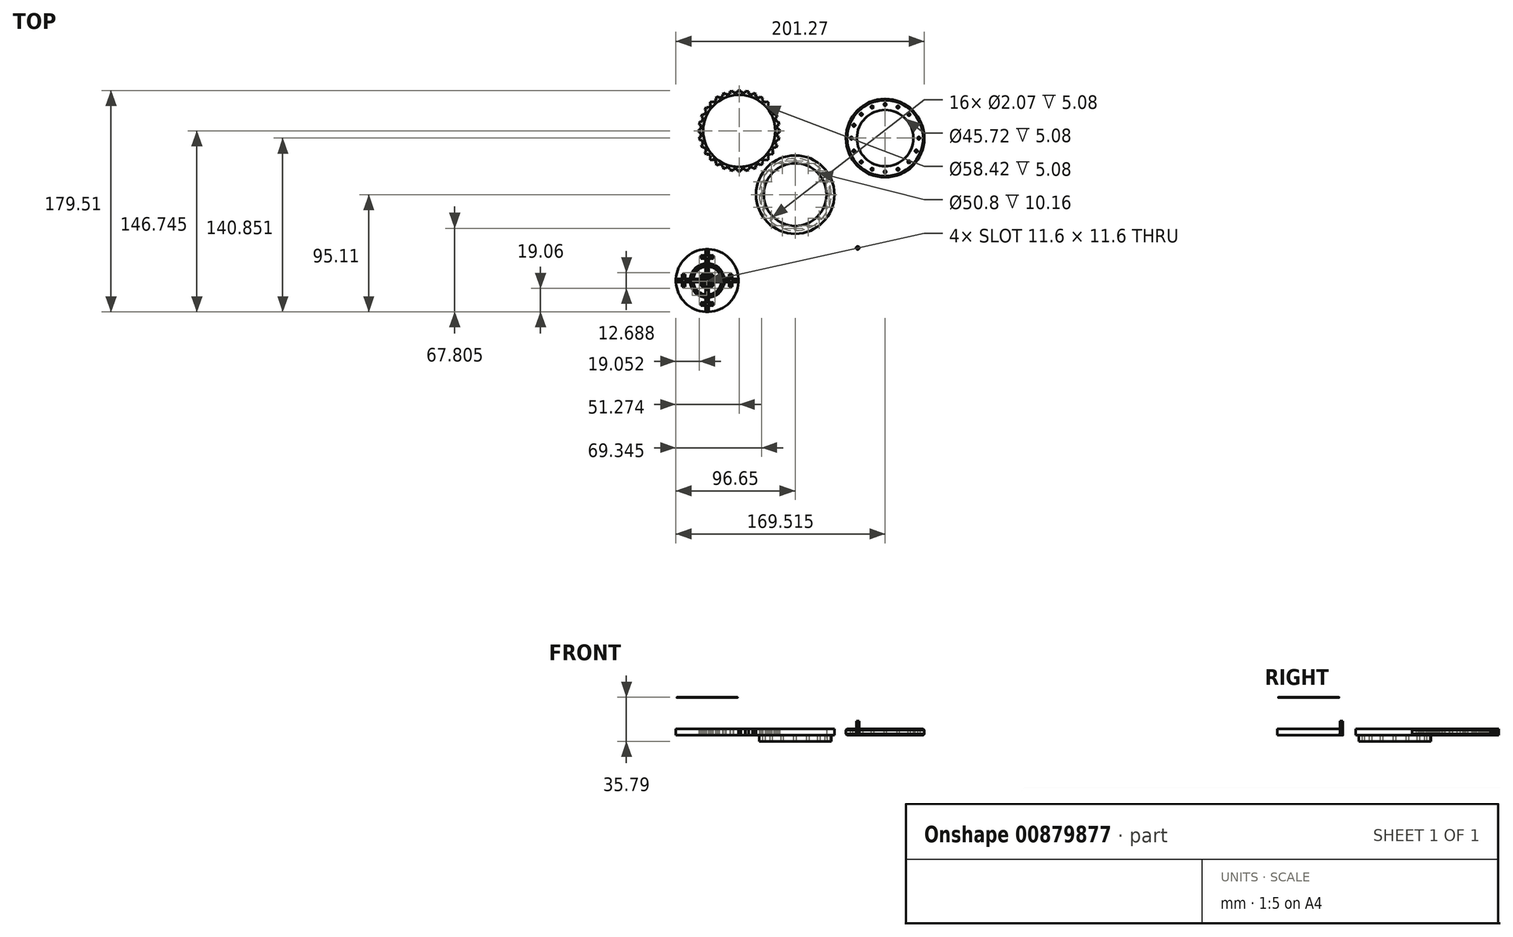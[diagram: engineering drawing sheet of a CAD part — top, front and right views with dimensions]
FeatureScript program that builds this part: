
annotation { "Feature Type Name" : "Feature", "Feature Type Description" : "" }
export const myFeature = defineFeature(function(context is Context, id is Id, definition is map)
    precondition{}
    {
        {
            var Q0;
            Q0=qCreatedBy(makeId("Top.planeOp"),FACE);
            var sketch = newSketch(context, id + "F0", { "sketchPlane" : qUnion([Q0])});
            skCircle(sketch, "E0", {"center": v(0, 0) * mm, "radius": 25.4 * mm});
            skCircle(sketch, "E1", {"center": v(0, 0) * mm, "radius": 31.75 * mm});
            skSolve(sketch);
        }
        {
            var Q0;
            Q0 = qSketchRegion(id + "F0", true);
            extrude(context, id + "F1", {"entities" : qUnion([Q0]), "depth" : 5.08 * mm, "offsetDistance" : 25.4 * mm});
        }
        {
            var Q0;
            Q0=makeQuery(id+"F1.opExtrude","CAP_FACE",FACE,{"disambiguationData":[OSD([sQuery(id+"F0.wireOp",EDGE,"E0"),sQuery(id+"F0.wireOp",EDGE,"E1")])],"isStart":true});
            var sketch = newSketch(context, id + "F2", { "sketchPlane" : qUnion([Q0])});
            skCircle(sketch, "E2", {"center": v(0, 0) * mm, "radius": 29.21 * mm});
            skCircle(sketch, "E3", {"center": v(27.3, 0) * mm, "radius": 1.04 * mm});
            skLineSegment(sketch, "E4", {"start": v(27.3, 0) * mm, "end": v(28.34, 0) * mm});
            skLineSegment(sketch, "E5", {"start": v(29.21, 0) * mm, "end": v(25.4, 0) * mm});
            skLineSegment(sketch, "E6.trimOffspring", {"start": v(25.4, 0) * mm, "end": v(29.21, 0) * mm});
            skCircle(sketch, "E7.1.0", {"center": v(25.23, 10.45) * mm, "radius": 1.04 * mm});
            skCircle(sketch, "E7.2.0", {"center": v(19.3, 19.3) * mm, "radius": 1.04 * mm});
            skCircle(sketch, "E7.3.0", {"center": v(10.45, 25.23) * mm, "radius": 1.04 * mm});
            skCircle(sketch, "E7.4.0", {"center": v(0, 27.3) * mm, "radius": 1.04 * mm});
            skCircle(sketch, "E7.5.0", {"center": v(-10.45, 25.23) * mm, "radius": 1.04 * mm});
            skCircle(sketch, "E7.6.0", {"center": v(-19.3, 19.3) * mm, "radius": 1.04 * mm});
            skCircle(sketch, "E7.7.0", {"center": v(-25.23, 10.45) * mm, "radius": 1.04 * mm});
            skCircle(sketch, "E7.8.0", {"center": v(-27.3, 0) * mm, "radius": 1.04 * mm});
            skCircle(sketch, "E7.9.0", {"center": v(-25.23, -10.45) * mm, "radius": 1.04 * mm});
            skCircle(sketch, "E7.10.0", {"center": v(-19.3, -19.3) * mm, "radius": 1.04 * mm});
            skCircle(sketch, "E7.11.0", {"center": v(-10.45, -25.23) * mm, "radius": 1.04 * mm});
            skCircle(sketch, "E7.12.0", {"center": v(0, -27.3) * mm, "radius": 1.04 * mm});
            skCircle(sketch, "E7.13.0", {"center": v(10.45, -25.23) * mm, "radius": 1.04 * mm});
            skCircle(sketch, "E7.14.0", {"center": v(19.3, -19.3) * mm, "radius": 1.04 * mm});
            skCircle(sketch, "E7.15.0", {"center": v(25.23, -10.45) * mm, "radius": 1.04 * mm});
            skSolve(sketch);
        }
        {
            var Q0;
            Q0=makeQuery(id+"F2.imprint","IMPRINT",FACE,{"disambiguationData":[TD([[makeQuery(id+"F2.imprint","IMPRINT",EDGE,{"derivedFrom":sQuery(id+"F2.wireOp",EDGE,"E2")}),1.0]])]});
            extrude(context, id + "F3", {"entities" : qUnion([Q0]), "operationType" : NewBodyOperationType.ADD, "depth" : 5.08 * mm, "offsetDistance" : 25.4 * mm});
        }
        {
            var Q0;
            Q0=qCreatedBy(makeId("Top.planeOp"),FACE);
            var sketch = newSketch(context, id + "F4", { "sketchPlane" : qUnion([Q0])});
            skCircle(sketch, "E8", {"center": v(-45.38, 51.63) * mm, "radius": 29.21 * mm});
            skCircle(sketch, "E9", {"center": v(-45.38, 51.63) * mm, "radius": 31.12 * mm});
            skLineSegment(sketch, "E10.bottom", {"start": v(-46.65, 81.86) * mm, "end": v(-44.1, 81.86) * mm});
            skLineSegment(sketch, "E10.top", {"start": v(-46.65, 84.4) * mm, "end": v(-44.1, 84.4) * mm});
            skLineSegment(sketch, "E10.left", {"start": v(-44.1, 81.86) * mm, "end": v(-44.1, 84.4) * mm});
            skLineSegment(sketch, "E10.right", {"start": v(-46.65, 81.86) * mm, "end": v(-46.65, 84.4) * mm});
            skLineSegment(sketch, "E11", {"start": v(-45.38, 51.63) * mm, "end": v(-45.38, 82.75) * mm, "construction": true});
            skLineSegment(sketch, "E12", {"start": v(-45.38, 80.84) * mm, "end": v(-45.38, 82.75) * mm, "construction": true});
            skLineSegment(sketch, "E13.1.0", {"start": v(-53.01, 83.52) * mm, "end": v(-50.52, 84.02) * mm});
            skLineSegment(sketch, "E13.1.1", {"start": v(-50.03, 81.53) * mm, "end": v(-50.52, 84.02) * mm});
            skLineSegment(sketch, "E13.1.2", {"start": v(-52.52, 81.03) * mm, "end": v(-53.01, 83.52) * mm});
            skLineSegment(sketch, "E13.2.0", {"start": v(-59.09, 81.42) * mm, "end": v(-56.74, 82.4) * mm});
            skLineSegment(sketch, "E13.2.1", {"start": v(-55.77, 80.05) * mm, "end": v(-56.74, 82.4) * mm});
            skLineSegment(sketch, "E13.2.2", {"start": v(-58.12, 79.07) * mm, "end": v(-59.09, 81.42) * mm});
            skLineSegment(sketch, "E13.3.0", {"start": v(-64.64, 78.17) * mm, "end": v(-62.52, 79.58) * mm});
            skLineSegment(sketch, "E13.3.1", {"start": v(-61.11, 77.47) * mm, "end": v(-62.52, 79.58) * mm});
            skLineSegment(sketch, "E13.3.2", {"start": v(-63.22, 76.06) * mm, "end": v(-64.64, 78.17) * mm});
            skLineSegment(sketch, "E13.4.0", {"start": v(-69.44, 73.9) * mm, "end": v(-67.65, 75.7) * mm});
            skLineSegment(sketch, "E13.4.1", {"start": v(-65.85, 73.9) * mm, "end": v(-67.65, 75.7) * mm});
            skLineSegment(sketch, "E13.4.2", {"start": v(-67.65, 72.1) * mm, "end": v(-69.44, 73.9) * mm});
            skLineSegment(sketch, "E13.5.0", {"start": v(-73.33, 68.78) * mm, "end": v(-71.91, 70.9) * mm});
            skLineSegment(sketch, "E13.5.1", {"start": v(-69.8, 69.48) * mm, "end": v(-71.91, 70.9) * mm});
            skLineSegment(sketch, "E13.5.2", {"start": v(-71.21, 67.37) * mm, "end": v(-73.33, 68.78) * mm});
            skLineSegment(sketch, "E13.6.0", {"start": v(-76.13, 63) * mm, "end": v(-75.16, 65.35) * mm});
            skLineSegment(sketch, "E13.6.1", {"start": v(-72.82, 64.37) * mm, "end": v(-75.16, 65.35) * mm});
            skLineSegment(sketch, "E13.6.2", {"start": v(-73.79, 62.03) * mm, "end": v(-76.13, 63) * mm});
            skLineSegment(sketch, "E13.7.0", {"start": v(-77.76, 56.78) * mm, "end": v(-77.26, 59.27) * mm});
            skLineSegment(sketch, "E13.7.1", {"start": v(-74.77, 58.78) * mm, "end": v(-77.26, 59.27) * mm});
            skLineSegment(sketch, "E13.7.2", {"start": v(-75.27, 56.29) * mm, "end": v(-77.76, 56.78) * mm});
            skLineSegment(sketch, "E13.8.0", {"start": v(-78.14, 50.36) * mm, "end": v(-78.14, 52.9) * mm});
            skLineSegment(sketch, "E13.8.1", {"start": v(-75.6, 52.9) * mm, "end": v(-78.14, 52.9) * mm});
            skLineSegment(sketch, "E13.8.2", {"start": v(-75.6, 50.36) * mm, "end": v(-78.14, 50.36) * mm});
            skLineSegment(sketch, "E13.9.0", {"start": v(-77.26, 44) * mm, "end": v(-77.76, 46.49) * mm});
            skLineSegment(sketch, "E13.9.1", {"start": v(-75.27, 46.98) * mm, "end": v(-77.76, 46.49) * mm});
            skLineSegment(sketch, "E13.9.2", {"start": v(-74.77, 44.5) * mm, "end": v(-77.26, 44) * mm});
            skLineSegment(sketch, "E13.10.0", {"start": v(-75.16, 37.92) * mm, "end": v(-76.13, 40.27) * mm});
            skLineSegment(sketch, "E13.10.1", {"start": v(-73.79, 41.24) * mm, "end": v(-76.13, 40.27) * mm});
            skLineSegment(sketch, "E13.10.2", {"start": v(-72.82, 38.9) * mm, "end": v(-75.16, 37.92) * mm});
            skLineSegment(sketch, "E13.11.0", {"start": v(-71.91, 32.37) * mm, "end": v(-73.33, 34.49) * mm});
            skLineSegment(sketch, "E13.11.1", {"start": v(-71.21, 35.9) * mm, "end": v(-73.33, 34.49) * mm});
            skLineSegment(sketch, "E13.11.2", {"start": v(-69.8, 33.79) * mm, "end": v(-71.91, 32.37) * mm});
            skLineSegment(sketch, "E13.12.0", {"start": v(-67.65, 27.57) * mm, "end": v(-69.44, 29.36) * mm});
            skLineSegment(sketch, "E13.12.1", {"start": v(-67.65, 31.16) * mm, "end": v(-69.44, 29.36) * mm});
            skLineSegment(sketch, "E13.12.2", {"start": v(-65.85, 29.36) * mm, "end": v(-67.65, 27.57) * mm});
            skLineSegment(sketch, "E13.13.0", {"start": v(-62.52, 23.69) * mm, "end": v(-64.64, 25.1) * mm});
            skLineSegment(sketch, "E13.13.1", {"start": v(-63.22, 27.2) * mm, "end": v(-64.64, 25.1) * mm});
            skLineSegment(sketch, "E13.13.2", {"start": v(-61.11, 25.8) * mm, "end": v(-62.52, 23.69) * mm});
            skLineSegment(sketch, "E13.14.0", {"start": v(-56.74, 20.88) * mm, "end": v(-59.09, 21.85) * mm});
            skLineSegment(sketch, "E13.14.1", {"start": v(-58.12, 24.2) * mm, "end": v(-59.09, 21.85) * mm});
            skLineSegment(sketch, "E13.14.2", {"start": v(-55.77, 23.22) * mm, "end": v(-56.74, 20.88) * mm});
            skLineSegment(sketch, "E13.15.0", {"start": v(-50.52, 19.25) * mm, "end": v(-53.01, 19.75) * mm});
            skLineSegment(sketch, "E13.15.1", {"start": v(-52.52, 22.24) * mm, "end": v(-53.01, 19.75) * mm});
            skLineSegment(sketch, "E13.15.2", {"start": v(-50.03, 21.74) * mm, "end": v(-50.52, 19.25) * mm});
            skLineSegment(sketch, "E13.16.0", {"start": v(-44.1, 18.87) * mm, "end": v(-46.65, 18.87) * mm});
            skLineSegment(sketch, "E13.16.1", {"start": v(-46.65, 21.4) * mm, "end": v(-46.65, 18.87) * mm});
            skLineSegment(sketch, "E13.16.2", {"start": v(-44.1, 21.4) * mm, "end": v(-44.1, 18.87) * mm});
            skLineSegment(sketch, "E13.17.0", {"start": v(-37.74, 19.75) * mm, "end": v(-40.23, 19.25) * mm});
            skLineSegment(sketch, "E13.17.1", {"start": v(-40.72, 21.74) * mm, "end": v(-40.23, 19.25) * mm});
            skLineSegment(sketch, "E13.17.2", {"start": v(-38.23, 22.24) * mm, "end": v(-37.74, 19.75) * mm});
            skLineSegment(sketch, "E13.18.0", {"start": v(-31.66, 21.85) * mm, "end": v(-34.01, 20.88) * mm});
            skLineSegment(sketch, "E13.18.1", {"start": v(-34.98, 23.22) * mm, "end": v(-34.01, 20.88) * mm});
            skLineSegment(sketch, "E13.18.2", {"start": v(-32.64, 24.2) * mm, "end": v(-31.66, 21.85) * mm});
            skLineSegment(sketch, "E13.19.0", {"start": v(-26.12, 25.1) * mm, "end": v(-28.23, 23.69) * mm});
            skLineSegment(sketch, "E13.19.1", {"start": v(-29.64, 25.8) * mm, "end": v(-28.23, 23.69) * mm});
            skLineSegment(sketch, "E13.19.2", {"start": v(-27.53, 27.2) * mm, "end": v(-26.12, 25.1) * mm});
            skLineSegment(sketch, "E13.20.0", {"start": v(-21.3, 29.36) * mm, "end": v(-23.1, 27.57) * mm});
            skLineSegment(sketch, "E13.20.1", {"start": v(-24.9, 29.36) * mm, "end": v(-23.1, 27.57) * mm});
            skLineSegment(sketch, "E13.20.2", {"start": v(-23.1, 31.16) * mm, "end": v(-21.3, 29.36) * mm});
            skLineSegment(sketch, "E13.21.0", {"start": v(-17.43, 34.49) * mm, "end": v(-18.84, 32.37) * mm});
            skLineSegment(sketch, "E13.21.1", {"start": v(-20.95, 33.79) * mm, "end": v(-18.84, 32.37) * mm});
            skLineSegment(sketch, "E13.21.2", {"start": v(-19.54, 35.9) * mm, "end": v(-17.43, 34.49) * mm});
            skLineSegment(sketch, "E13.22.0", {"start": v(-14.62, 40.27) * mm, "end": v(-15.6, 37.92) * mm});
            skLineSegment(sketch, "E13.22.1", {"start": v(-17.94, 38.9) * mm, "end": v(-15.6, 37.92) * mm});
            skLineSegment(sketch, "E13.22.2", {"start": v(-16.96, 41.24) * mm, "end": v(-14.62, 40.27) * mm});
            skLineSegment(sketch, "E13.23.0", {"start": v(-13, 46.49) * mm, "end": v(-13.49, 44) * mm});
            skLineSegment(sketch, "E13.23.1", {"start": v(-15.98, 44.5) * mm, "end": v(-13.49, 44) * mm});
            skLineSegment(sketch, "E13.23.2", {"start": v(-15.48, 46.98) * mm, "end": v(-13, 46.49) * mm});
            skLineSegment(sketch, "E13.24.0", {"start": v(-12.6, 52.9) * mm, "end": v(-12.6, 50.36) * mm});
            skLineSegment(sketch, "E13.24.1", {"start": v(-15.15, 50.36) * mm, "end": v(-12.6, 50.36) * mm});
            skLineSegment(sketch, "E13.24.2", {"start": v(-15.15, 52.9) * mm, "end": v(-12.6, 52.9) * mm});
            skLineSegment(sketch, "E13.25.0", {"start": v(-13.49, 59.27) * mm, "end": v(-13, 56.78) * mm});
            skLineSegment(sketch, "E13.25.1", {"start": v(-15.48, 56.29) * mm, "end": v(-13, 56.78) * mm});
            skLineSegment(sketch, "E13.25.2", {"start": v(-15.98, 58.78) * mm, "end": v(-13.49, 59.27) * mm});
            skLineSegment(sketch, "E13.26.0", {"start": v(-15.6, 65.35) * mm, "end": v(-14.62, 63) * mm});
            skLineSegment(sketch, "E13.26.1", {"start": v(-16.96, 62.03) * mm, "end": v(-14.62, 63) * mm});
            skLineSegment(sketch, "E13.26.2", {"start": v(-17.94, 64.37) * mm, "end": v(-15.6, 65.35) * mm});
            skLineSegment(sketch, "E13.27.0", {"start": v(-18.84, 70.9) * mm, "end": v(-17.43, 68.78) * mm});
            skLineSegment(sketch, "E13.27.1", {"start": v(-19.54, 67.37) * mm, "end": v(-17.43, 68.78) * mm});
            skLineSegment(sketch, "E13.27.2", {"start": v(-20.95, 69.48) * mm, "end": v(-18.84, 70.9) * mm});
            skLineSegment(sketch, "E13.28.0", {"start": v(-23.1, 75.7) * mm, "end": v(-21.3, 73.9) * mm});
            skLineSegment(sketch, "E13.28.1", {"start": v(-23.1, 72.1) * mm, "end": v(-21.3, 73.9) * mm});
            skLineSegment(sketch, "E13.28.2", {"start": v(-24.9, 73.9) * mm, "end": v(-23.1, 75.7) * mm});
            skLineSegment(sketch, "E13.29.0", {"start": v(-28.23, 79.58) * mm, "end": v(-26.12, 78.17) * mm});
            skLineSegment(sketch, "E13.29.1", {"start": v(-27.53, 76.06) * mm, "end": v(-26.12, 78.17) * mm});
            skLineSegment(sketch, "E13.29.2", {"start": v(-29.64, 77.47) * mm, "end": v(-28.23, 79.58) * mm});
            skLineSegment(sketch, "E13.30.0", {"start": v(-34.01, 82.4) * mm, "end": v(-31.66, 81.42) * mm});
            skLineSegment(sketch, "E13.30.1", {"start": v(-32.64, 79.07) * mm, "end": v(-31.66, 81.42) * mm});
            skLineSegment(sketch, "E13.30.2", {"start": v(-34.98, 80.05) * mm, "end": v(-34.01, 82.4) * mm});
            skLineSegment(sketch, "E13.31.0", {"start": v(-40.23, 84.02) * mm, "end": v(-37.74, 83.52) * mm});
            skLineSegment(sketch, "E13.31.1", {"start": v(-38.23, 81.03) * mm, "end": v(-37.74, 83.52) * mm});
            skLineSegment(sketch, "E13.31.2", {"start": v(-40.72, 81.53) * mm, "end": v(-40.23, 84.02) * mm});
            skSolve(sketch);
        }
        {
            var Q0;
            Q0 = qSketchRegion(id + "F4", true);
            extrude(context, id + "F5", {"entities" : qUnion([Q0]), "depth" : 5.08 * mm, "offsetDistance" : 25.4 * mm});
        }
        {
            var Q0;
            Q0=qCreatedBy(makeId("Top.planeOp"),FACE);
            var sketch = newSketch(context, id + "F6", { "sketchPlane" : qUnion([Q0])});
            skCircle(sketch, "E14", {"center": v(72.87, 45.74) * mm, "radius": 22.86 * mm});
            skCircle(sketch, "E15", {"center": v(72.87, 45.74) * mm, "radius": 31.75 * mm});
            skCircle(sketch, "E16", {"center": v(100.17, 45.74) * mm, "radius": 1.04 * mm});
            skLineSegment(sketch, "E17", {"start": v(72.87, 45.74) * mm, "end": v(143.46, 45.74) * mm, "construction": true});
            skCircle(sketch, "E18.1.0", {"center": v(98.1, 56.19) * mm, "radius": 1.04 * mm});
            skCircle(sketch, "E18.2.0", {"center": v(92.17, 65.05) * mm, "radius": 1.04 * mm});
            skCircle(sketch, "E18.3.0", {"center": v(83.31, 70.97) * mm, "radius": 1.04 * mm});
            skCircle(sketch, "E18.4.0", {"center": v(72.87, 73.05) * mm, "radius": 1.04 * mm});
            skCircle(sketch, "E18.5.0", {"center": v(62.42, 70.97) * mm, "radius": 1.04 * mm});
            skCircle(sketch, "E18.6.0", {"center": v(53.56, 65.05) * mm, "radius": 1.04 * mm});
            skCircle(sketch, "E18.7.0", {"center": v(47.64, 56.19) * mm, "radius": 1.04 * mm});
            skCircle(sketch, "E18.8.0", {"center": v(45.56, 45.74) * mm, "radius": 1.04 * mm});
            skCircle(sketch, "E18.9.0", {"center": v(47.64, 35.3) * mm, "radius": 1.04 * mm});
            skCircle(sketch, "E18.10.0", {"center": v(53.56, 26.43) * mm, "radius": 1.04 * mm});
            skCircle(sketch, "E18.11.0", {"center": v(62.42, 20.51) * mm, "radius": 1.04 * mm});
            skCircle(sketch, "E18.12.0", {"center": v(72.87, 18.44) * mm, "radius": 1.04 * mm});
            skCircle(sketch, "E18.13.0", {"center": v(83.31, 20.51) * mm, "radius": 1.04 * mm});
            skCircle(sketch, "E18.14.0", {"center": v(92.17, 26.43) * mm, "radius": 1.04 * mm});
            skCircle(sketch, "E18.15.0", {"center": v(98.1, 35.3) * mm, "radius": 1.04 * mm});
            skSolve(sketch);
        }
        {
            var Q0;
            Q0 = qSketchRegion(id + "F6", true);
            extrude(context, id + "F7", {"entities" : qUnion([Q0]), "depth" : 5.08 * mm, "offsetDistance" : 25.4 * mm});
        }
        {
            var Q0;
            Q0=makeQuery(id+"F7.opExtrude","CAP_EDGE",EDGE,{"disambiguationData":[OSD([sQuery(id+"F6.wireOp",EDGE,"E15")])],"isStart":false});
            var Q1;
            Q1=makeQuery(id+"F7.opExtrude","CAP_EDGE",EDGE,{"disambiguationData":[OSD([sQuery(id+"F6.wireOp",EDGE,"E15")])],"isStart":true});
            chamfer(context, id + "F8", {"entities" : qUnion([Q0, Q1]), "width" : 1.02 * mm, "tangentPropagation" : true});
        }
        {
            var Q0;
            Q0=qCreatedBy(makeId("Top.planeOp"),FACE);
            var sketch = newSketch(context, id + "F9", { "sketchPlane" : qUnion([Q0])});
            skCircle(sketch, "E19", {"center": v(-71.25, -69.7) * mm, "radius": 25.4 * mm});
            skSolve(sketch);
        }
        {
            var Q0;
            Q0 = qSketchRegion(id + "F9", true);
            extrude(context, id + "F10", {"entities" : qUnion([Q0]), "depth" : 5.08 * mm, "offsetDistance" : 25.4 * mm});
        }
        {
            var Q0;
            Q0=qCreatedBy(makeId("Top.planeOp"),FACE);
            var sketch = newSketch(context, id + "F11", { "sketchPlane" : qUnion([Q0])});
            skCircle(sketch, "E20", {"center": v(50.66, -43.23) * mm, "radius": 1.27 * mm});
            skSolve(sketch);
        }
        {
            var Q0;
            Q0 = qSketchRegion(id + "F11", true);
            extrude(context, id + "F12", {"entities" : qUnion([Q0]), "depth" : 1.27 * mm, "offsetDistance" : 25.4 * mm});
        }
        {
            var Q0;
            Q0=makeQuery(id+"F12.opExtrude","CAP_FACE",FACE,{"disambiguationData":[OSD([sQuery(id+"F11.wireOp",EDGE,"E20")])],"isStart":false});
            var sketch = newSketch(context, id + "F13", { "sketchPlane" : qUnion([Q0])});
            skCircle(sketch, "E21", {"center": v(50.66, -43.23) * mm, "radius": 1.04 * mm});
            skSolve(sketch);
        }
        {
            var Q0;
            Q0 = qSketchRegion(id + "F13", true);
            extrude(context, id + "F14", {"entities" : qUnion([Q0]), "operationType" : NewBodyOperationType.ADD, "depth" : 10.16 * mm, "offsetDistance" : 25.4 * mm});
        }
        {
            var Q0;
            Q0=makeQuery(id+"F10.opExtrude","CAP_FACE",FACE,{"disambiguationData":[OSD([sQuery(id+"F9.wireOp",EDGE,"E19")])],"isStart":false});
            var sketch = newSketch(context, id + "F15", { "sketchPlane" : qUnion([Q0])});
            skCircle(sketch, "E22", {"center": v(-71.25, -69.7) * mm, "radius": 13.97 * mm});
            skCircle(sketch, "E23", {"center": v(-71.25, -69.7) * mm, "radius": 11.43 * mm});
            skCircle(sketch, "E24", {"center": v(-71.25, -69.7) * mm, "radius": 6.35 * mm});
            skCircle(sketch, "E25", {"center": v(-71.25, -69.7) * mm, "radius": 3.81 * mm});
            skLineSegment(sketch, "E26", {"start": v(-71.25, -69.7) * mm, "end": v(-45.85, -69.7) * mm, "construction": true});
            skLineSegment(sketch, "E27", {"start": v(-71.25, -69.7) * mm, "end": v(-71.25, -44.3) * mm, "construction": true});
            skLineSegment(sketch, "E28", {"start": v(-69.98, -40.66) * mm, "end": v(-69.98, -101.53) * mm});
            skLineSegment(sketch, "E29.MirrorCS", {"start": v(-72.52, -40.66) * mm, "end": v(-72.52, -101.53) * mm});
            skLineSegment(sketch, "E30", {"start": v(-38.83, -68.44) * mm, "end": v(-103.24, -68.44) * mm});
            skLineSegment(sketch, "E31.MirrorCS", {"start": v(-38.83, -70.98) * mm, "end": v(-103.24, -70.98) * mm});
            skLineSegment(sketch, "E32.bottom", {"start": v(-91.57, -64.63) * mm, "end": v(-89.03, -64.63) * mm});
            skLineSegment(sketch, "E32.top", {"start": v(-91.57, -74.79) * mm, "end": v(-89.03, -74.79) * mm});
            skLineSegment(sketch, "E32.left", {"start": v(-91.57, -64.63) * mm, "end": v(-91.57, -74.79) * mm});
            skLineSegment(sketch, "E32.right", {"start": v(-89.03, -64.63) * mm, "end": v(-89.03, -74.79) * mm});
            skLineSegment(sketch, "E33.1.0", {"start": v(-76.33, -90.03) * mm, "end": v(-66.17, -90.03) * mm});
            skLineSegment(sketch, "E33.1.1", {"start": v(-66.17, -90.03) * mm, "end": v(-66.17, -87.49) * mm});
            skLineSegment(sketch, "E33.1.2", {"start": v(-76.33, -87.49) * mm, "end": v(-66.17, -87.49) * mm});
            skLineSegment(sketch, "E33.1.3", {"start": v(-76.33, -90.03) * mm, "end": v(-76.33, -87.49) * mm});
            skLineSegment(sketch, "E33.2.0", {"start": v(-50.93, -74.79) * mm, "end": v(-50.93, -64.63) * mm});
            skLineSegment(sketch, "E33.2.1", {"start": v(-50.93, -64.63) * mm, "end": v(-53.47, -64.63) * mm});
            skLineSegment(sketch, "E33.2.2", {"start": v(-53.47, -74.79) * mm, "end": v(-53.47, -64.63) * mm});
            skLineSegment(sketch, "E33.2.3", {"start": v(-50.93, -74.79) * mm, "end": v(-53.47, -74.79) * mm});
            skLineSegment(sketch, "E33.3.0", {"start": v(-66.17, -49.39) * mm, "end": v(-76.33, -49.39) * mm});
            skLineSegment(sketch, "E33.3.1", {"start": v(-76.33, -49.39) * mm, "end": v(-76.33, -51.93) * mm});
            skLineSegment(sketch, "E33.3.2", {"start": v(-66.17, -51.93) * mm, "end": v(-76.33, -51.93) * mm});
            skLineSegment(sketch, "E33.3.3", {"start": v(-66.17, -49.39) * mm, "end": v(-66.17, -51.93) * mm});
            skSolve(sketch);
        }
        {
            var Q0;
            {var subQ0=sQuery(id+"F15.wireOp",EDGE,"E32.left");var subQ1=sQuery(id+"F15.wireOp",EDGE,"E30");var subQ2=makeQuery(id+"F15.imprint","INTERSECT",VERTEX,{"derivedFrom":[subQ1,subQ0]});Q0=makeQuery(id+"F15.imprint","IMPRINT",FACE,{"disambiguationData":[TD([[makeQuery(id+"F15.imprint","IMPRINT",EDGE,{"disambiguationData":[TD([[subQ2,-1.0]])],"derivedFrom":subQ1}),1.0]])]});}
            var Q1;
            {var subQ0=sQuery(id+"F15.wireOp",EDGE,"E32.right");var subQ1=sQuery(id+"F15.wireOp",EDGE,"E30");var subQ2=makeQuery(id+"F15.imprint","INTERSECT",VERTEX,{"derivedFrom":[subQ1,subQ0]});Q1=makeQuery(id+"F15.imprint","IMPRINT",FACE,{"disambiguationData":[TD([[makeQuery(id+"F15.imprint","IMPRINT",EDGE,{"disambiguationData":[TD([[subQ2,-1.0]])],"derivedFrom":subQ1}),1.0]])]});}
            var Q2;
            {var subQ5=sQuery(id+"F15.wireOp",EDGE,"E32.top");Q2=makeQuery(id+"F15.imprint","IMPRINT",FACE,{"disambiguationData":[TD([[makeQuery(id+"F15.imprint","IMPRINT",EDGE,{"derivedFrom":subQ5}),1.0]])]});}
            var Q3;
            {var subQ5=sQuery(id+"F15.wireOp",EDGE,"E32.bottom");Q3=makeQuery(id+"F15.imprint","IMPRINT",FACE,{"disambiguationData":[TD([[makeQuery(id+"F15.imprint","IMPRINT",EDGE,{"derivedFrom":subQ5}),-1.0]])]});}
            var Q4;
            {var subQ0=sQuery(id+"F15.wireOp",EDGE,"E30");var subQ1=sQuery(id+"F15.wireOp",EDGE,"E22");var subQ2=makeQuery(id+"F15.imprint","INTERSECT",VERTEX,{"disambiguationData":[OD(1.0)],"derivedFrom":[subQ1,subQ0]});Q4=makeQuery(id+"F15.imprint","IMPRINT",FACE,{"disambiguationData":[TD([[makeQuery(id+"F15.imprint","IMPRINT",EDGE,{"disambiguationData":[TD([[subQ2,-1.0]])],"derivedFrom":subQ1}),-1.0]])]});}
            var Q5;
            {var subQ0=sQuery(id+"F15.wireOp",EDGE,"E30");var subQ1=sQuery(id+"F15.wireOp",EDGE,"E22");var subQ2=makeQuery(id+"F15.imprint","INTERSECT",VERTEX,{"disambiguationData":[OD(1.0)],"derivedFrom":[subQ1,subQ0]});Q5=makeQuery(id+"F15.imprint","IMPRINT",FACE,{"disambiguationData":[TD([[makeQuery(id+"F15.imprint","IMPRINT",EDGE,{"disambiguationData":[TD([[subQ2,-1.0]])],"derivedFrom":subQ1}),1.0]])]});}
            var Q6;
            {var subQ0=sQuery(id+"F15.wireOp",EDGE,"E31.MirrorCS");var subQ1=sQuery(id+"F15.wireOp",EDGE,"E22");var subQ2=makeQuery(id+"F15.imprint","INTERSECT",VERTEX,{"disambiguationData":[OD(0.0)],"derivedFrom":[subQ1,subQ0]});Q6=makeQuery(id+"F15.imprint","IMPRINT",FACE,{"disambiguationData":[TD([[makeQuery(id+"F15.imprint","IMPRINT",EDGE,{"disambiguationData":[TD([[subQ2,-1.0]])],"derivedFrom":subQ1}),1.0]])]});}
            var Q7;
            {var subQ0=sQuery(id+"F15.wireOp",EDGE,"E30");var subQ1=sQuery(id+"F15.wireOp",EDGE,"E23");var subQ2=makeQuery(id+"F15.imprint","INTERSECT",VERTEX,{"disambiguationData":[OD(1.0)],"derivedFrom":[subQ1,subQ0]});Q7=makeQuery(id+"F15.imprint","IMPRINT",FACE,{"disambiguationData":[TD([[makeQuery(id+"F15.imprint","IMPRINT",EDGE,{"disambiguationData":[TD([[subQ2,-1.0]])],"derivedFrom":subQ1}),1.0]])]});}
            var Q8;
            {var subQ0=sQuery(id+"F15.wireOp",EDGE,"E29.MirrorCS");var subQ1=sQuery(id+"F15.wireOp",EDGE,"E22");var subQ2=makeQuery(id+"F15.imprint","INTERSECT",VERTEX,{"disambiguationData":[OD(0.0)],"derivedFrom":[subQ1,subQ0]});Q8=makeQuery(id+"F15.imprint","IMPRINT",FACE,{"disambiguationData":[TD([[makeQuery(id+"F15.imprint","IMPRINT",EDGE,{"disambiguationData":[TD([[subQ2,-1.0]])],"derivedFrom":subQ1}),1.0]])]});}
            var Q9;
            {var subQ0=sQuery(id+"F15.wireOp",EDGE,"E31.MirrorCS");var subQ1=sQuery(id+"F15.wireOp",EDGE,"E24");var subQ2=makeQuery(id+"F15.imprint","INTERSECT",VERTEX,{"disambiguationData":[OD(0.0)],"derivedFrom":[subQ1,subQ0]});Q9=makeQuery(id+"F15.imprint","IMPRINT",FACE,{"disambiguationData":[TD([[makeQuery(id+"F15.imprint","IMPRINT",EDGE,{"disambiguationData":[TD([[subQ2,-1.0]])],"derivedFrom":subQ1}),1.0]])]});}
            var Q10;
            {var subQ0=sQuery(id+"F15.wireOp",EDGE,"E29.MirrorCS");var subQ1=sQuery(id+"F15.wireOp",EDGE,"E24");var subQ2=makeQuery(id+"F15.imprint","INTERSECT",VERTEX,{"disambiguationData":[OD(1.0)],"derivedFrom":[subQ1,subQ0]});Q10=makeQuery(id+"F15.imprint","IMPRINT",FACE,{"disambiguationData":[TD([[makeQuery(id+"F15.imprint","IMPRINT",EDGE,{"disambiguationData":[TD([[subQ2,-1.0]])],"derivedFrom":subQ1}),1.0]])]});}
            var Q11;
            {var subQ0=sQuery(id+"F15.wireOp",EDGE,"E29.MirrorCS");var subQ1=sQuery(id+"F15.wireOp",EDGE,"E22");var subQ2=makeQuery(id+"F15.imprint","INTERSECT",VERTEX,{"disambiguationData":[OD(1.0)],"derivedFrom":[subQ1,subQ0]});Q11=makeQuery(id+"F15.imprint","IMPRINT",FACE,{"disambiguationData":[TD([[makeQuery(id+"F15.imprint","IMPRINT",EDGE,{"disambiguationData":[TD([[subQ2,-1.0]])],"derivedFrom":subQ1}),1.0]])]});}
            var Q12;
            {var subQ5=sQuery(id+"F15.wireOp",EDGE,"E33.1.3");Q12=makeQuery(id+"F15.imprint","IMPRINT",FACE,{"disambiguationData":[TD([[makeQuery(id+"F15.imprint","IMPRINT",EDGE,{"derivedFrom":subQ5}),-1.0]])]});}
            var Q13;
            {var subQ5=sQuery(id+"F15.wireOp",EDGE,"E33.1.1");Q13=makeQuery(id+"F15.imprint","IMPRINT",FACE,{"disambiguationData":[TD([[makeQuery(id+"F15.imprint","IMPRINT",EDGE,{"derivedFrom":subQ5}),1.0]])]});}
            var Q14;
            {var subQ0=sQuery(id+"F15.wireOp",EDGE,"E29.MirrorCS");var subQ1=sQuery(id+"F15.wireOp",EDGE,"E22");var subQ2=makeQuery(id+"F15.imprint","INTERSECT",VERTEX,{"disambiguationData":[OD(1.0)],"derivedFrom":[subQ1,subQ0]});Q14=makeQuery(id+"F15.imprint","IMPRINT",FACE,{"disambiguationData":[TD([[makeQuery(id+"F15.imprint","IMPRINT",EDGE,{"disambiguationData":[TD([[subQ2,-1.0]])],"derivedFrom":subQ1}),-1.0]])]});}
            var Q15;
            {var subQ0=sQuery(id+"F15.wireOp",EDGE,"E33.1.0");var subQ1=sQuery(id+"F15.wireOp",EDGE,"E28");var subQ2=makeQuery(id+"F15.imprint","INTERSECT",VERTEX,{"derivedFrom":[subQ1,subQ0]});Q15=makeQuery(id+"F15.imprint","IMPRINT",FACE,{"disambiguationData":[TD([[makeQuery(id+"F15.imprint","IMPRINT",EDGE,{"disambiguationData":[TD([[subQ2,-1.0]])],"derivedFrom":subQ1}),-1.0]])]});}
            var Q16;
            {var subQ0=sQuery(id+"F15.wireOp",EDGE,"E33.1.2");var subQ1=sQuery(id+"F15.wireOp",EDGE,"E28");var subQ2=makeQuery(id+"F15.imprint","INTERSECT",VERTEX,{"derivedFrom":[subQ1,subQ0]});Q16=makeQuery(id+"F15.imprint","IMPRINT",FACE,{"disambiguationData":[TD([[makeQuery(id+"F15.imprint","IMPRINT",EDGE,{"disambiguationData":[TD([[subQ2,-1.0]])],"derivedFrom":subQ1}),-1.0]])]});}
            var Q17;
            {var subQ0=sQuery(id+"F15.wireOp",EDGE,"E28");var subQ1=sQuery(id+"F15.wireOp",EDGE,"E22");var subQ2=makeQuery(id+"F15.imprint","INTERSECT",VERTEX,{"disambiguationData":[OD(1.0)],"derivedFrom":[subQ1,subQ0]});Q17=makeQuery(id+"F15.imprint","IMPRINT",FACE,{"disambiguationData":[TD([[makeQuery(id+"F15.imprint","IMPRINT",EDGE,{"disambiguationData":[TD([[subQ2,-1.0]])],"derivedFrom":subQ1}),1.0]])]});}
            var Q18;
            {var subQ5=sQuery(id+"F15.wireOp",EDGE,"E33.2.3");Q18=makeQuery(id+"F15.imprint","IMPRINT",FACE,{"disambiguationData":[TD([[makeQuery(id+"F15.imprint","IMPRINT",EDGE,{"derivedFrom":subQ5}),-1.0]])]});}
            var Q19;
            {var subQ0=sQuery(id+"F15.wireOp",EDGE,"E33.2.0");var subQ1=sQuery(id+"F15.wireOp",EDGE,"E30");var subQ2=makeQuery(id+"F15.imprint","INTERSECT",VERTEX,{"derivedFrom":[subQ1,subQ0]});Q19=makeQuery(id+"F15.imprint","IMPRINT",FACE,{"disambiguationData":[TD([[makeQuery(id+"F15.imprint","IMPRINT",EDGE,{"disambiguationData":[TD([[subQ2,1.0]])],"derivedFrom":subQ1}),1.0]])]});}
            var Q20;
            {var subQ0=sQuery(id+"F15.wireOp",EDGE,"E33.2.0");var subQ1=sQuery(id+"F15.wireOp",EDGE,"E30");var subQ2=makeQuery(id+"F15.imprint","INTERSECT",VERTEX,{"derivedFrom":[subQ1,subQ0]});Q20=makeQuery(id+"F15.imprint","IMPRINT",FACE,{"disambiguationData":[TD([[makeQuery(id+"F15.imprint","IMPRINT",EDGE,{"disambiguationData":[TD([[subQ2,-1.0]])],"derivedFrom":subQ1}),1.0]])]});}
            var Q21;
            {var subQ5=sQuery(id+"F15.wireOp",EDGE,"E33.2.1");Q21=makeQuery(id+"F15.imprint","IMPRINT",FACE,{"disambiguationData":[TD([[makeQuery(id+"F15.imprint","IMPRINT",EDGE,{"derivedFrom":subQ5}),1.0]])]});}
            var Q22;
            {var subQ0=sQuery(id+"F15.wireOp",EDGE,"E30");var subQ1=sQuery(id+"F15.wireOp",EDGE,"E22");var subQ2=makeQuery(id+"F15.imprint","INTERSECT",VERTEX,{"disambiguationData":[OD(0.0)],"derivedFrom":[subQ1,subQ0]});Q22=makeQuery(id+"F15.imprint","IMPRINT",FACE,{"disambiguationData":[TD([[makeQuery(id+"F15.imprint","IMPRINT",EDGE,{"disambiguationData":[TD([[subQ2,1.0]])],"derivedFrom":subQ1}),-1.0]])]});}
            var Q23;
            {var subQ0=sQuery(id+"F15.wireOp",EDGE,"E30");var subQ1=sQuery(id+"F15.wireOp",EDGE,"E22");var subQ2=makeQuery(id+"F15.imprint","INTERSECT",VERTEX,{"disambiguationData":[OD(0.0)],"derivedFrom":[subQ1,subQ0]});Q23=makeQuery(id+"F15.imprint","IMPRINT",FACE,{"disambiguationData":[TD([[makeQuery(id+"F15.imprint","IMPRINT",EDGE,{"disambiguationData":[TD([[subQ2,1.0]])],"derivedFrom":subQ1}),1.0]])]});}
            var Q24;
            {var subQ0=sQuery(id+"F15.wireOp",EDGE,"E28");var subQ1=sQuery(id+"F15.wireOp",EDGE,"E22");var subQ2=makeQuery(id+"F15.imprint","INTERSECT",VERTEX,{"disambiguationData":[OD(0.0)],"derivedFrom":[subQ1,subQ0]});Q24=makeQuery(id+"F15.imprint","IMPRINT",FACE,{"disambiguationData":[TD([[makeQuery(id+"F15.imprint","IMPRINT",EDGE,{"disambiguationData":[TD([[subQ2,1.0]])],"derivedFrom":subQ1}),1.0]])]});}
            var Q25;
            {var subQ0=sQuery(id+"F15.wireOp",EDGE,"E28");var subQ1=sQuery(id+"F15.wireOp",EDGE,"E24");var subQ2=makeQuery(id+"F15.imprint","INTERSECT",VERTEX,{"disambiguationData":[OD(1.0)],"derivedFrom":[subQ1,subQ0]});Q25=makeQuery(id+"F15.imprint","IMPRINT",FACE,{"disambiguationData":[TD([[makeQuery(id+"F15.imprint","IMPRINT",EDGE,{"disambiguationData":[TD([[subQ2,-1.0]])],"derivedFrom":subQ1}),1.0]])]});}
            var Q26;
            {var subQ0=sQuery(id+"F15.wireOp",EDGE,"E30");var subQ1=sQuery(id+"F15.wireOp",EDGE,"E24");var subQ2=makeQuery(id+"F15.imprint","INTERSECT",VERTEX,{"disambiguationData":[OD(1.0)],"derivedFrom":[subQ1,subQ0]});Q26=makeQuery(id+"F15.imprint","IMPRINT",FACE,{"disambiguationData":[TD([[makeQuery(id+"F15.imprint","IMPRINT",EDGE,{"disambiguationData":[TD([[subQ2,-1.0]])],"derivedFrom":subQ1}),1.0]])]});}
            var Q27;
            {var subQ0=sQuery(id+"F15.wireOp",EDGE,"E29.MirrorCS");var subQ1=sQuery(id+"F15.wireOp",EDGE,"E24");var subQ2=makeQuery(id+"F15.imprint","INTERSECT",VERTEX,{"disambiguationData":[OD(0.0)],"derivedFrom":[subQ1,subQ0]});Q27=makeQuery(id+"F15.imprint","IMPRINT",FACE,{"disambiguationData":[TD([[makeQuery(id+"F15.imprint","IMPRINT",EDGE,{"disambiguationData":[TD([[subQ2,-1.0]])],"derivedFrom":subQ1}),1.0]])]});}
            var Q28;
            {var subQ0=sQuery(id+"F15.wireOp",EDGE,"E29.MirrorCS");var subQ1=sQuery(id+"F15.wireOp",EDGE,"E25");var subQ2=makeQuery(id+"F15.imprint","INTERSECT",VERTEX,{"disambiguationData":[OD(1.0)],"derivedFrom":[subQ1,subQ0]});Q28=makeQuery(id+"F15.imprint","IMPRINT",FACE,{"disambiguationData":[TD([[makeQuery(id+"F15.imprint","IMPRINT",EDGE,{"disambiguationData":[TD([[subQ2,-1.0]])],"derivedFrom":subQ1}),1.0]])]});}
            var Q29;
            {var subQ0=sQuery(id+"F15.wireOp",EDGE,"E30");var subQ1=sQuery(id+"F15.wireOp",EDGE,"E25");var subQ2=makeQuery(id+"F15.imprint","INTERSECT",VERTEX,{"disambiguationData":[OD(0.0)],"derivedFrom":[subQ1,subQ0]});Q29=makeQuery(id+"F15.imprint","IMPRINT",FACE,{"disambiguationData":[TD([[makeQuery(id+"F15.imprint","IMPRINT",EDGE,{"disambiguationData":[TD([[subQ2,1.0]])],"derivedFrom":subQ1}),1.0]])]});}
            var Q30;
            {var subQ0=sQuery(id+"F15.wireOp",EDGE,"E30");var subQ1=sQuery(id+"F15.wireOp",EDGE,"E28");var subQ2=makeQuery(id+"F15.imprint","INTERSECT",VERTEX,{"derivedFrom":[subQ1,subQ0]});Q30=makeQuery(id+"F15.imprint","IMPRINT",FACE,{"disambiguationData":[TD([[makeQuery(id+"F15.imprint","IMPRINT",EDGE,{"disambiguationData":[TD([[subQ2,-1.0]])],"derivedFrom":subQ1}),-1.0]])]});}
            var Q31;
            {var subQ0=sQuery(id+"F15.wireOp",EDGE,"E30");var subQ1=sQuery(id+"F15.wireOp",EDGE,"E25");var subQ2=makeQuery(id+"F15.imprint","INTERSECT",VERTEX,{"disambiguationData":[OD(1.0)],"derivedFrom":[subQ1,subQ0]});Q31=makeQuery(id+"F15.imprint","IMPRINT",FACE,{"disambiguationData":[TD([[makeQuery(id+"F15.imprint","IMPRINT",EDGE,{"disambiguationData":[TD([[subQ2,-1.0]])],"derivedFrom":subQ1}),1.0]])]});}
            var Q32;
            {var subQ0=sQuery(id+"F15.wireOp",EDGE,"E28");var subQ1=sQuery(id+"F15.wireOp",EDGE,"E25");var subQ2=makeQuery(id+"F15.imprint","INTERSECT",VERTEX,{"disambiguationData":[OD(0.0)],"derivedFrom":[subQ1,subQ0]});Q32=makeQuery(id+"F15.imprint","IMPRINT",FACE,{"disambiguationData":[TD([[makeQuery(id+"F15.imprint","IMPRINT",EDGE,{"disambiguationData":[TD([[subQ2,-1.0]])],"derivedFrom":subQ1}),1.0]])]});}
            var Q33;
            {var subQ0=sQuery(id+"F15.wireOp",EDGE,"E28");var subQ1=sQuery(id+"F15.wireOp",EDGE,"E24");var subQ2=makeQuery(id+"F15.imprint","INTERSECT",VERTEX,{"disambiguationData":[OD(0.0)],"derivedFrom":[subQ1,subQ0]});Q33=makeQuery(id+"F15.imprint","IMPRINT",FACE,{"disambiguationData":[TD([[makeQuery(id+"F15.imprint","IMPRINT",EDGE,{"disambiguationData":[TD([[subQ2,-1.0]])],"derivedFrom":subQ1}),1.0]])]});}
            var Q34;
            {var subQ0=sQuery(id+"F15.wireOp",EDGE,"E28");var subQ1=sQuery(id+"F15.wireOp",EDGE,"E23");var subQ2=makeQuery(id+"F15.imprint","INTERSECT",VERTEX,{"disambiguationData":[OD(0.0)],"derivedFrom":[subQ1,subQ0]});Q34=makeQuery(id+"F15.imprint","IMPRINT",FACE,{"disambiguationData":[TD([[makeQuery(id+"F15.imprint","IMPRINT",EDGE,{"disambiguationData":[TD([[subQ2,-1.0]])],"derivedFrom":subQ1}),1.0]])]});}
            var Q35;
            {var subQ0=sQuery(id+"F15.wireOp",EDGE,"E30");var subQ1=sQuery(id+"F15.wireOp",EDGE,"E23");var subQ2=makeQuery(id+"F15.imprint","INTERSECT",VERTEX,{"disambiguationData":[OD(0.0)],"derivedFrom":[subQ1,subQ0]});Q35=makeQuery(id+"F15.imprint","IMPRINT",FACE,{"disambiguationData":[TD([[makeQuery(id+"F15.imprint","IMPRINT",EDGE,{"disambiguationData":[TD([[subQ2,1.0]])],"derivedFrom":subQ1}),1.0]])]});}
            var Q36;
            {var subQ0=sQuery(id+"F15.wireOp",EDGE,"E30");var subQ1=sQuery(id+"F15.wireOp",EDGE,"E24");var subQ2=makeQuery(id+"F15.imprint","INTERSECT",VERTEX,{"disambiguationData":[OD(0.0)],"derivedFrom":[subQ1,subQ0]});Q36=makeQuery(id+"F15.imprint","IMPRINT",FACE,{"disambiguationData":[TD([[makeQuery(id+"F15.imprint","IMPRINT",EDGE,{"disambiguationData":[TD([[subQ2,1.0]])],"derivedFrom":subQ1}),1.0]])]});}
            var Q37;
            {var subQ0=sQuery(id+"F15.wireOp",EDGE,"E28");var subQ1=sQuery(id+"F15.wireOp",EDGE,"E24");var subQ2=makeQuery(id+"F15.imprint","INTERSECT",VERTEX,{"disambiguationData":[OD(0.0)],"derivedFrom":[subQ1,subQ0]});Q37=makeQuery(id+"F15.imprint","IMPRINT",FACE,{"disambiguationData":[TD([[makeQuery(id+"F15.imprint","IMPRINT",EDGE,{"disambiguationData":[TD([[subQ2,1.0]])],"derivedFrom":subQ1}),1.0]])]});}
            var Q38;
            {var subQ0=sQuery(id+"F15.wireOp",EDGE,"E28");var subQ1=sQuery(id+"F15.wireOp",EDGE,"E22");var subQ2=makeQuery(id+"F15.imprint","INTERSECT",VERTEX,{"disambiguationData":[OD(0.0)],"derivedFrom":[subQ1,subQ0]});Q38=makeQuery(id+"F15.imprint","IMPRINT",FACE,{"disambiguationData":[TD([[makeQuery(id+"F15.imprint","IMPRINT",EDGE,{"disambiguationData":[TD([[subQ2,-1.0]])],"derivedFrom":subQ1}),1.0]])]});}
            var Q39;
            {var subQ0=sQuery(id+"F15.wireOp",EDGE,"E33.3.0");var subQ1=sQuery(id+"F15.wireOp",EDGE,"E28");var subQ2=makeQuery(id+"F15.imprint","INTERSECT",VERTEX,{"derivedFrom":[subQ1,subQ0]});Q39=makeQuery(id+"F15.imprint","IMPRINT",FACE,{"disambiguationData":[TD([[makeQuery(id+"F15.imprint","IMPRINT",EDGE,{"disambiguationData":[TD([[subQ2,-1.0]])],"derivedFrom":subQ1}),-1.0]])]});}
            var Q40;
            {var subQ5=sQuery(id+"F15.wireOp",EDGE,"E33.3.3");Q40=makeQuery(id+"F15.imprint","IMPRINT",FACE,{"disambiguationData":[TD([[makeQuery(id+"F15.imprint","IMPRINT",EDGE,{"derivedFrom":subQ5}),-1.0]])]});}
            var Q41;
            {var subQ5=sQuery(id+"F15.wireOp",EDGE,"E33.3.1");Q41=makeQuery(id+"F15.imprint","IMPRINT",FACE,{"disambiguationData":[TD([[makeQuery(id+"F15.imprint","IMPRINT",EDGE,{"derivedFrom":subQ5}),1.0]])]});}
            var Q42;
            {var subQ0=sQuery(id+"F15.wireOp",EDGE,"E29.MirrorCS");var subQ1=sQuery(id+"F15.wireOp",EDGE,"E23");var subQ2=makeQuery(id+"F15.imprint","INTERSECT",VERTEX,{"disambiguationData":[OD(1.0)],"derivedFrom":[subQ1,subQ0]});Q42=makeQuery(id+"F15.imprint","IMPRINT",FACE,{"disambiguationData":[TD([[makeQuery(id+"F15.imprint","IMPRINT",EDGE,{"disambiguationData":[TD([[subQ2,-1.0]])],"derivedFrom":subQ1}),1.0]])]});}
            var Q43;
            {var subQ0=sQuery(id+"F15.wireOp",EDGE,"E28");var subQ1=sQuery(id+"F15.wireOp",EDGE,"E22");var subQ2=makeQuery(id+"F15.imprint","INTERSECT",VERTEX,{"disambiguationData":[OD(0.0)],"derivedFrom":[subQ1,subQ0]});Q43=makeQuery(id+"F15.imprint","IMPRINT",FACE,{"disambiguationData":[TD([[makeQuery(id+"F15.imprint","IMPRINT",EDGE,{"disambiguationData":[TD([[subQ2,-1.0]])],"derivedFrom":subQ1}),-1.0]])]});}
            var Q44;
            {var subQ0=sQuery(id+"F15.wireOp",EDGE,"E33.3.0");var subQ1=sQuery(id+"F15.wireOp",EDGE,"E28");var subQ2=makeQuery(id+"F15.imprint","INTERSECT",VERTEX,{"derivedFrom":[subQ1,subQ0]});Q44=makeQuery(id+"F15.imprint","IMPRINT",FACE,{"disambiguationData":[TD([[makeQuery(id+"F15.imprint","IMPRINT",EDGE,{"disambiguationData":[TD([[subQ2,1.0]])],"derivedFrom":subQ1}),-1.0]])]});}
            extrude(context, id + "F16", {"entities" : qUnion([Q0, Q1, Q2, Q3, Q4, Q5, Q6, Q7, Q8, Q9, Q10, Q11, Q12, Q13, Q14, Q15, Q16, Q17, Q18, Q19, Q20, Q21, Q22, Q23, Q24, Q25, Q26, Q27, Q28, Q29, Q30, Q31, Q32, Q33, Q34, Q35, Q36, Q37, Q38, Q39, Q40, Q41, Q42, Q43, Q44]), "operationType" : NewBodyOperationType.REMOVE, "oppositeDirection" : true, "depth" : 0.03 * mm, "offsetDistance" : 25.4 * mm, "hasDraft" : true, "draftAngle" : 88 * degree, "draftPullDirection" : true});
        }
        {
            var Q0;
            Q0=makeQuery(id+"F16.boolean.opBoolean","COPY",FACE,{"derivedFrom":makeQuery(id+"F16.opExtrude","CAP_FACE",FACE,{"disambiguationData":[OSD([sQuery(id+"F9.wireOp",EDGE,"E19"),sQuery(id+"F15.wireOp",EDGE,"E22"),sQuery(id+"F15.wireOp",EDGE,"E23"),sQuery(id+"F15.wireOp",EDGE,"E24"),sQuery(id+"F15.wireOp",EDGE,"E25"),sQuery(id+"F15.wireOp",EDGE,"E28"),sQuery(id+"F15.wireOp",EDGE,"E29.MirrorCS"),sQuery(id+"F15.wireOp",EDGE,"E30"),sQuery(id+"F15.wireOp",EDGE,"E31.MirrorCS"),sQuery(id+"F15.wireOp",EDGE,"E32.bottom"),sQuery(id+"F15.wireOp",EDGE,"E32.top"),sQuery(id+"F15.wireOp",EDGE,"E32.left"),sQuery(id+"F15.wireOp",EDGE,"E32.right"),sQuery(id+"F15.wireOp",EDGE,"E33.1.0"),sQuery(id+"F15.wireOp",EDGE,"E33.1.1"),sQuery(id+"F15.wireOp",EDGE,"E33.1.2"),sQuery(id+"F15.wireOp",EDGE,"E33.1.3"),sQuery(id+"F15.wireOp",EDGE,"E33.2.0"),sQuery(id+"F15.wireOp",EDGE,"E33.2.1"),sQuery(id+"F15.wireOp",EDGE,"E33.2.2"),sQuery(id+"F15.wireOp",EDGE,"E33.2.3"),sQuery(id+"F15.wireOp",EDGE,"E33.3.0"),sQuery(id+"F15.wireOp",EDGE,"E33.3.1"),sQuery(id+"F15.wireOp",EDGE,"E33.3.2"),sQuery(id+"F15.wireOp",EDGE,"E33.3.3")])],"isStart":false})});
            var sketch = newSketch(context, id + "F17", { "sketchPlane" : qUnion([Q0])});
            skSolve(sketch);
        }
        {
            var Q0;
            {var subQ78=sQuery(id+"F15.wireOp",EDGE,"E32.bottom");Q0=makeQuery(id+"F17.imprint","IMPRINT",FACE,{"disambiguationData":[TD([[makeQuery(id+"F17.imprint","IMPRINT",EDGE,{"derivedFrom":makeQuery(id+"F16.boolean.opBoolean","COPY",EDGE,{"derivedFrom":makeQuery(id+"F16.opExtrude","CAP_EDGE",EDGE,{"disambiguationData":[OSD([subQ78])],"isStart":false})})}),-1.0]])]});}
            extrude(context, id + "F18", {"entities" : qUnion([Q0]), "depth" : 0.25 * mm, "offsetDistance" : 25.4 * mm, "hasDraft" : true, "draftAngle" : 30 * degree, "draftPullDirection" : true});
        }
        {
            var Q0;
            Q0=makeQuery(id+"F18.opExtrude","SWEPT_BODY",BODY,{"disambiguationData":[OSD([sQuery(id+"F9.wireOp",EDGE,"E19"),sQuery(id+"F15.wireOp",EDGE,"E22"),sQuery(id+"F15.wireOp",EDGE,"E23"),sQuery(id+"F15.wireOp",EDGE,"E24"),sQuery(id+"F15.wireOp",EDGE,"E25"),sQuery(id+"F15.wireOp",EDGE,"E28"),sQuery(id+"F15.wireOp",EDGE,"E29.MirrorCS"),sQuery(id+"F15.wireOp",EDGE,"E30"),sQuery(id+"F15.wireOp",EDGE,"E31.MirrorCS"),sQuery(id+"F15.wireOp",EDGE,"E32.bottom"),sQuery(id+"F15.wireOp",EDGE,"E32.top"),sQuery(id+"F15.wireOp",EDGE,"E32.left"),sQuery(id+"F15.wireOp",EDGE,"E32.right"),sQuery(id+"F15.wireOp",EDGE,"E33.1.0"),sQuery(id+"F15.wireOp",EDGE,"E33.1.1"),sQuery(id+"F15.wireOp",EDGE,"E33.1.2"),sQuery(id+"F15.wireOp",EDGE,"E33.1.3"),sQuery(id+"F15.wireOp",EDGE,"E33.2.0"),sQuery(id+"F15.wireOp",EDGE,"E33.2.1"),sQuery(id+"F15.wireOp",EDGE,"E33.2.2"),sQuery(id+"F15.wireOp",EDGE,"E33.2.3"),sQuery(id+"F15.wireOp",EDGE,"E33.3.0"),sQuery(id+"F15.wireOp",EDGE,"E33.3.1"),sQuery(id+"F15.wireOp",EDGE,"E33.3.2"),sQuery(id+"F15.wireOp",EDGE,"E33.3.3")])]});
            var Q1;
            Q1=qCreatedBy(makeId("Top.planeOp"),FACE);
            transform(context, id + "F19", {"entities" : qUnion([Q0]), "transformType" : TransformType.TRANSLATION_DISTANCE, "transformDirection" : qUnion([Q1]), "distance" : 25.4 * mm, "makeCopy" : true});
        }
        {
            var Q0;
            Q0=makeQuery(id+"F18.opExtrude","SWEPT_BODY",BODY,{"disambiguationData":[OSD([sQuery(id+"F9.wireOp",EDGE,"E19"),sQuery(id+"F15.wireOp",EDGE,"E22"),sQuery(id+"F15.wireOp",EDGE,"E23"),sQuery(id+"F15.wireOp",EDGE,"E24"),sQuery(id+"F15.wireOp",EDGE,"E25"),sQuery(id+"F15.wireOp",EDGE,"E28"),sQuery(id+"F15.wireOp",EDGE,"E29.MirrorCS"),sQuery(id+"F15.wireOp",EDGE,"E30"),sQuery(id+"F15.wireOp",EDGE,"E31.MirrorCS"),sQuery(id+"F15.wireOp",EDGE,"E32.bottom"),sQuery(id+"F15.wireOp",EDGE,"E32.top"),sQuery(id+"F15.wireOp",EDGE,"E32.left"),sQuery(id+"F15.wireOp",EDGE,"E32.right"),sQuery(id+"F15.wireOp",EDGE,"E33.1.0"),sQuery(id+"F15.wireOp",EDGE,"E33.1.1"),sQuery(id+"F15.wireOp",EDGE,"E33.1.2"),sQuery(id+"F15.wireOp",EDGE,"E33.1.3"),sQuery(id+"F15.wireOp",EDGE,"E33.2.0"),sQuery(id+"F15.wireOp",EDGE,"E33.2.1"),sQuery(id+"F15.wireOp",EDGE,"E33.2.2"),sQuery(id+"F15.wireOp",EDGE,"E33.2.3"),sQuery(id+"F15.wireOp",EDGE,"E33.3.0"),sQuery(id+"F15.wireOp",EDGE,"E33.3.1"),sQuery(id+"F15.wireOp",EDGE,"E33.3.2"),sQuery(id+"F15.wireOp",EDGE,"E33.3.3")])]});
            deleteBodies(context, id + "F20", {"entities" : qUnion([Q0])});
        }
    });
